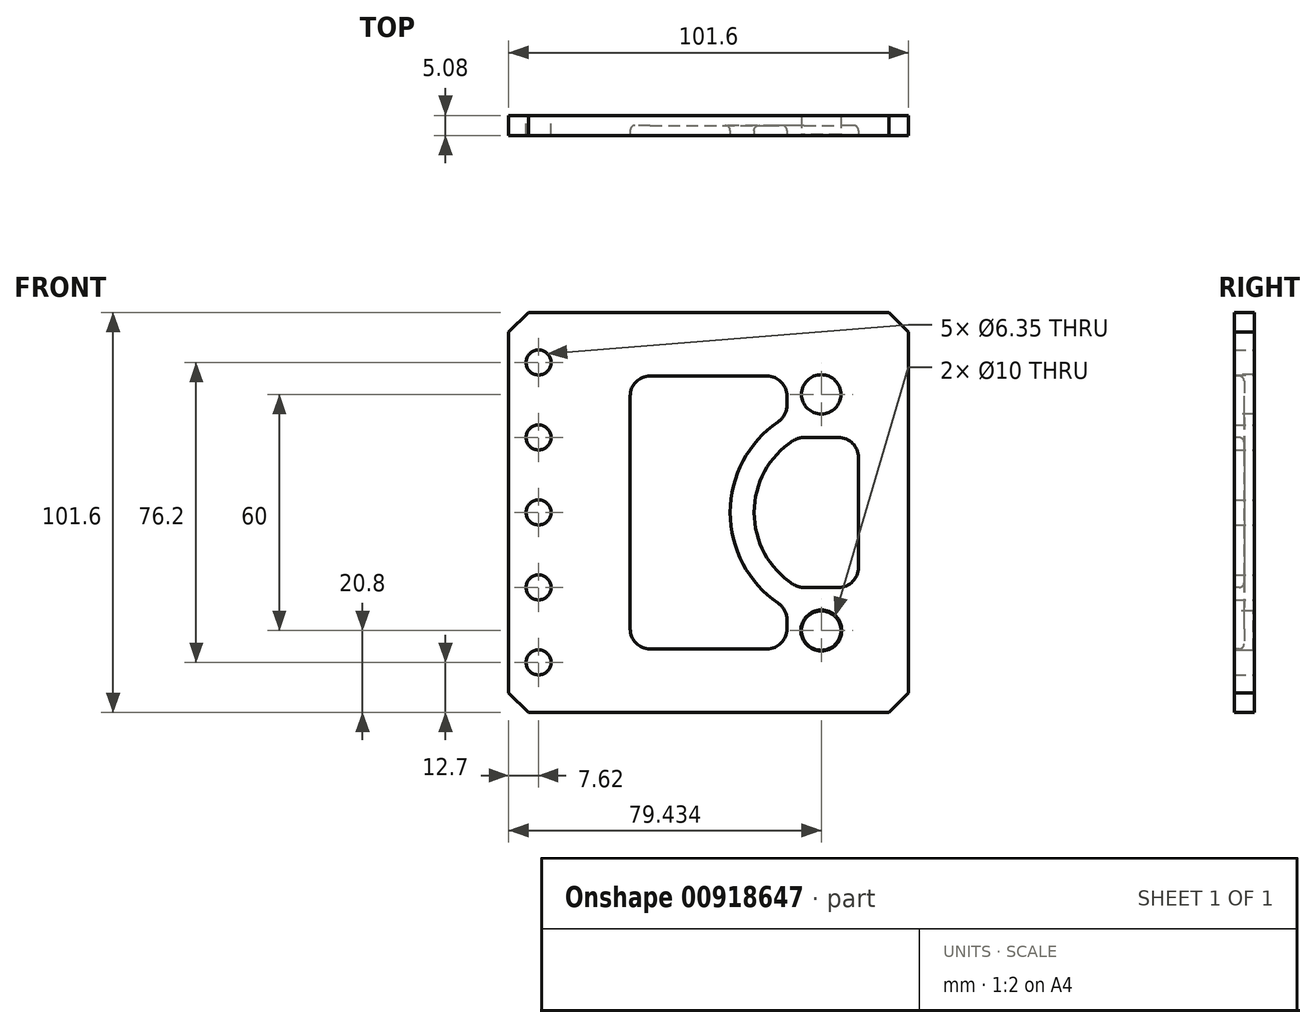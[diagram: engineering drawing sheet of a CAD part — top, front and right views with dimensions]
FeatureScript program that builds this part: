
annotation { "Feature Type Name" : "Feature", "Feature Type Description" : "" }
export const myFeature = defineFeature(function(context is Context, id is Id, definition is map)
    precondition{}
    {
        {
            var Q0;
            Q0=qCreatedBy(makeId("Front.planeOp"),FACE);
            var sketch = newSketch(context, id + "F0", { "sketchPlane" : qUnion([Q0])});
            skLineSegment(sketch, "E0.bottom", {"start": v(-50.8, -50.8) * mm, "end": v(50.8, -50.8) * mm});
            skLineSegment(sketch, "E0.top", {"start": v(-50.8, 50.8) * mm, "end": v(50.8, 50.8) * mm});
            skLineSegment(sketch, "E0.left", {"start": v(-50.8, -50.8) * mm, "end": v(-50.8, 50.8) * mm});
            skLineSegment(sketch, "E0.right", {"start": v(50.8, -50.8) * mm, "end": v(50.8, 50.8) * mm});
            skPoint(sketch, "E0.middle", {"position": v(0, 0) * mm});
            skSolve(sketch);
        }
        {
            var Q0;
            Q0 = qSketchRegion(id + "F0", true);
            extrude(context, id + "F1", {"entities" : qUnion([Q0]), "depth" : 5.08 * mm, "offsetDistance" : 25.4 * mm});
        }
        {
            var Q0;
            Q0=qCreatedBy(makeId("Front.planeOp"),FACE);
            var sketch = newSketch(context, id + "F2", { "sketchPlane" : qUnion([Q0])});
            skPoint(sketch, "E1", {"position": v(-43.18, 38.1) * mm});
            skPoint(sketch, "E2", {"position": v(-43.18, 19.05) * mm});
            skPoint(sketch, "E3", {"position": v(-43.18, 0) * mm});
            skPoint(sketch, "E4", {"position": v(-43.18, -19.05) * mm});
            skPoint(sketch, "E5", {"position": v(-43.18, -38.1) * mm});
            skLineSegment(sketch, "E6", {"start": v(-43.18, 38.1) * mm, "end": v(-43.18, 19.05) * mm, "construction": true});
            skLineSegment(sketch, "E7", {"start": v(-43.18, 19.05) * mm, "end": v(-43.18, 0) * mm, "construction": true});
            skLineSegment(sketch, "E8", {"start": v(-43.18, 0) * mm, "end": v(-43.18, -19.05) * mm, "construction": true});
            skLineSegment(sketch, "E9", {"start": v(-43.18, -19.05) * mm, "end": v(-43.18, -38.1) * mm, "construction": true});
            skSolve(sketch);
        }
        {
            var Q0;
            Q0=sQuery(id+"F2.wireOp",VERTEX,"E5");
            var Q1;
            Q1=sQuery(id+"F2.wireOp",VERTEX,"E4");
            var Q2;
            Q2=sQuery(id+"F2.wireOp",VERTEX,"E3");
            var Q3;
            Q3=sQuery(id+"F2.wireOp",VERTEX,"E2");
            var Q4;
            Q4=sQuery(id+"F2.wireOp",VERTEX,"E1");
            var Q5;
            Q5=makeQuery(id+"F1.opExtrude","SWEPT_BODY",BODY,{"disambiguationData":[OSD([sQuery(id+"F0.wireOp",EDGE,"E0.bottom"),sQuery(id+"F0.wireOp",EDGE,"E0.top"),sQuery(id+"F0.wireOp",EDGE,"E0.left"),sQuery(id+"F0.wireOp",EDGE,"E0.right")])]});
            hole(context, id + "F3", {"style" : HoleStyle.SIMPLE, "endStyle" : HoleEndStyle.THROUGH, "oppositeDirection" : true, "holeDiameter" : 6.35 * mm, "majorDiameter" : 6.35 * mm, "isTappedThrough" : true, "tappedDepth" : 12.7 * mm, "tapClearance" : 3, "locations" : qUnion([Q0, Q1, Q2, Q3, Q4]), "scope" : qUnion([Q5])});
        }
        {
            var Q0;
            Q0=makeQuery(id+"F1.opExtrude","CAP_FACE",FACE,{"disambiguationData":[OSD([sQuery(id+"F0.wireOp",EDGE,"E0.bottom"),sQuery(id+"F0.wireOp",EDGE,"E0.top"),sQuery(id+"F0.wireOp",EDGE,"E0.left"),sQuery(id+"F0.wireOp",EDGE,"E0.right")])],"isStart":false});
            var sketch = newSketch(context, id + "F4", { "sketchPlane" : qUnion([Q0])});
            skLineSegment(sketch, "E10.bottom", {"start": v(-19.92, -34.67) * mm, "end": v(19.92, -34.67) * mm});
            skLineSegment(sketch, "E10.top", {"start": v(-19.92, 34.67) * mm, "end": v(19.92, 34.67) * mm});
            skLineSegment(sketch, "E10.left", {"start": v(-19.92, -34.67) * mm, "end": v(-19.92, 34.67) * mm});
            skLineSegment(sketch, "E10.right", {"start": v(19.92, -34.67) * mm, "end": v(19.92, -24.4) * mm});
            skPoint(sketch, "E10.middle", {"position": v(0, 0) * mm});
            skArc(sketch, "E11", {"start": v(19.92, 24.4) * mm, "mid": v(5.49, 0) * mm, "end": v(19.92, -24.4) * mm});
            skLineSegment(sketch, "E12.trimOffspring", {"start": v(19.92, 24.4) * mm, "end": v(19.92, 34.67) * mm});
            skSolve(sketch);
        }
        {
            var Q0;
            Q0 = qSketchRegion(id + "F4", true);
            extrude(context, id + "F5", {"entities" : qUnion([Q0]), "operationType" : NewBodyOperationType.REMOVE, "oppositeDirection" : true, "depth" : 2.54 * mm, "offsetDistance" : 25.4 * mm});
        }
        {
            var Q0;
            Q0=makeQuery(id+"F5.boolean.opBoolean","COPY",EDGE,{"derivedFrom":makeQuery(id+"F5.opExtrude","SWEPT_EDGE",EDGE,{"disambiguationData":[OSD([sQuery(id+"F4.wireOp",EDGE,"E10.top"),sQuery(id+"F4.wireOp",EDGE,"E10.left")])]})});
            var Q1;
            Q1=makeQuery(id+"F5.boolean.opBoolean","COPY",EDGE,{"derivedFrom":makeQuery(id+"F5.opExtrude","SWEPT_EDGE",EDGE,{"disambiguationData":[OSD([sQuery(id+"F4.wireOp",EDGE,"E10.top"),sQuery(id+"F4.wireOp",EDGE,"E12.trimOffspring")])]})});
            var Q2;
            Q2=makeQuery(id+"F5.boolean.opBoolean","COPY",EDGE,{"derivedFrom":makeQuery(id+"F5.opExtrude","SWEPT_EDGE",EDGE,{"disambiguationData":[OSD([sQuery(id+"F4.wireOp",EDGE,"E11"),sQuery(id+"F4.wireOp",EDGE,"E12.trimOffspring")])]})});
            var Q3;
            Q3=makeQuery(id+"F5.boolean.opBoolean","COPY",EDGE,{"derivedFrom":makeQuery(id+"F5.opExtrude","SWEPT_EDGE",EDGE,{"disambiguationData":[OSD([sQuery(id+"F4.wireOp",EDGE,"E10.right"),sQuery(id+"F4.wireOp",EDGE,"E11")])]})});
            var Q4;
            Q4=makeQuery(id+"F5.boolean.opBoolean","COPY",EDGE,{"derivedFrom":makeQuery(id+"F5.opExtrude","SWEPT_EDGE",EDGE,{"disambiguationData":[OSD([sQuery(id+"F4.wireOp",EDGE,"E10.bottom"),sQuery(id+"F4.wireOp",EDGE,"E10.right")])]})});
            var Q5;
            Q5=makeQuery(id+"F5.boolean.opBoolean","COPY",EDGE,{"derivedFrom":makeQuery(id+"F5.opExtrude","SWEPT_EDGE",EDGE,{"disambiguationData":[OSD([sQuery(id+"F4.wireOp",EDGE,"E10.bottom"),sQuery(id+"F4.wireOp",EDGE,"E10.left")])]})});
            fillet(context, id + "F6", {"entities" : qUnion([Q0, Q1, Q2, Q3, Q4, Q5]), "radius" : 5.08 * mm, "tangentPropagation" : true, "allowEdgeOverflow" : false});
        }
        {
            var Q0;
            Q0=makeQuery(id+"F5.boolean.opBoolean","COPY",FACE,{"derivedFrom":makeQuery(id+"F5.opExtrude","CAP_FACE",FACE,{"disambiguationData":[OSD([sQuery(id+"F4.wireOp",EDGE,"E10.bottom"),sQuery(id+"F4.wireOp",EDGE,"E10.top"),sQuery(id+"F4.wireOp",EDGE,"E10.left"),sQuery(id+"F4.wireOp",EDGE,"E10.right"),sQuery(id+"F4.wireOp",EDGE,"E11"),sQuery(id+"F4.wireOp",EDGE,"E12.trimOffspring")])],"isStart":false})});
            fillet(context, id + "F7", {"entities" : qUnion([Q0]), "radius" : 1.27 * mm, "tangentPropagation" : true, "allowEdgeOverflow" : false});
        }
        {
            var Q0;
            Q0=makeQuery(id+"F1.opExtrude","CAP_FACE",FACE,{"disambiguationData":[OSD([sQuery(id+"F0.wireOp",EDGE,"E0.bottom"),sQuery(id+"F0.wireOp",EDGE,"E0.top"),sQuery(id+"F0.wireOp",EDGE,"E0.left"),sQuery(id+"F0.wireOp",EDGE,"E0.right")])],"isStart":false});
            var sketch = newSketch(context, id + "F8", { "sketchPlane" : qUnion([Q0])});
            skArc(sketch, "E13.0", {"start": v(22.85, 19.05) * mm, "mid": v(11.58, 0) * mm, "end": v(22.85, -19.05) * mm});
            skLineSegment(sketch, "E14", {"start": v(22.85, 19.05) * mm, "end": v(38.1, 19.05) * mm});
            skLineSegment(sketch, "E15", {"start": v(38.1, 19.05) * mm, "end": v(38.1, -19.05) * mm});
            skLineSegment(sketch, "E16", {"start": v(38.1, -19.05) * mm, "end": v(22.85, -19.05) * mm});
            skSolve(sketch);
        }
        {
            var Q0;
            Q0 = qSketchRegion(id + "F8", true);
            extrude(context, id + "F9", {"entities" : qUnion([Q0]), "operationType" : NewBodyOperationType.REMOVE, "oppositeDirection" : true, "depth" : 2.54 * mm, "offsetDistance" : 25.4 * mm});
        }
        {
            var Q0;
            Q0=makeQuery(id+"F9.boolean.opBoolean","COPY",EDGE,{"derivedFrom":makeQuery(id+"F9.opExtrude","SWEPT_EDGE",EDGE,{"disambiguationData":[OSD([sQuery(id+"F8.wireOp",EDGE,"E13.0"),sQuery(id+"F8.wireOp",EDGE,"E14")])]})});
            var Q1;
            Q1=makeQuery(id+"F9.boolean.opBoolean","COPY",EDGE,{"derivedFrom":makeQuery(id+"F9.opExtrude","SWEPT_EDGE",EDGE,{"disambiguationData":[OSD([sQuery(id+"F8.wireOp",EDGE,"E14"),sQuery(id+"F8.wireOp",EDGE,"E15")])]})});
            var Q2;
            Q2=makeQuery(id+"F9.boolean.opBoolean","COPY",EDGE,{"derivedFrom":makeQuery(id+"F9.opExtrude","SWEPT_EDGE",EDGE,{"disambiguationData":[OSD([sQuery(id+"F8.wireOp",EDGE,"E15"),sQuery(id+"F8.wireOp",EDGE,"E16")])]})});
            var Q3;
            Q3=makeQuery(id+"F9.boolean.opBoolean","COPY",EDGE,{"derivedFrom":makeQuery(id+"F9.opExtrude","SWEPT_EDGE",EDGE,{"disambiguationData":[OSD([sQuery(id+"F8.wireOp",EDGE,"E13.0"),sQuery(id+"F8.wireOp",EDGE,"E16")])]})});
            fillet(context, id + "F10", {"entities" : qUnion([Q0, Q1, Q2, Q3]), "radius" : 5.08 * mm, "tangentPropagation" : true, "allowEdgeOverflow" : false});
        }
        {
            var Q0;
            Q0=makeQuery(id+"F9.boolean.opBoolean","COPY",FACE,{"derivedFrom":makeQuery(id+"F9.opExtrude","CAP_FACE",FACE,{"disambiguationData":[OSD([sQuery(id+"F8.wireOp",EDGE,"E13.0"),sQuery(id+"F8.wireOp",EDGE,"E14"),sQuery(id+"F8.wireOp",EDGE,"E15"),sQuery(id+"F8.wireOp",EDGE,"E16")])],"isStart":false})});
            fillet(context, id + "F11", {"entities" : qUnion([Q0]), "radius" : 1.27 * mm, "tangentPropagation" : true, "allowEdgeOverflow" : false});
        }
        {
            var Q0;
            Q0=makeQuery(id+"F1.opExtrude","CAP_FACE",FACE,{"disambiguationData":[OSD([sQuery(id+"F0.wireOp",EDGE,"E0.bottom"),sQuery(id+"F0.wireOp",EDGE,"E0.top"),sQuery(id+"F0.wireOp",EDGE,"E0.left"),sQuery(id+"F0.wireOp",EDGE,"E0.right")])],"isStart":false});
            var sketch = newSketch(context, id + "F12", { "sketchPlane" : qUnion([Q0])});
            skCircle(sketch, "E17", {"center": v(28.63, 30) * mm, "radius": 5 * mm});
            skCircle(sketch, "E18", {"center": v(28.63, -30) * mm, "radius": 5 * mm});
            skPoint(sketch, "E18.centerSnap0", {"position": v(28.63, -19.05) * mm});
            skLineSegment(sketch, "E19.0.1", {"start": v(-50.8, 50.8) * mm, "end": v(-50.8, -50.8) * mm, "construction": true});
            skLineSegment(sketch, "E19.0.2", {"start": v(-50.8, -50.8) * mm, "end": v(50.8, -50.8) * mm, "construction": true});
            skLineSegment(sketch, "E19.0.3", {"start": v(50.8, -50.8) * mm, "end": v(50.8, 50.8) * mm, "construction": true});
            skLineSegment(sketch, "E20", {"start": v(28.63, 30) * mm, "end": v(28.63, 0) * mm, "construction": true});
            skLineSegment(sketch, "E21", {"start": v(28.63, 0) * mm, "end": v(28.63, -30) * mm, "construction": true});
            skSolve(sketch);
        }
        {
            var Q0;
            Q0 = qSketchRegion(id + "F12", true);
            extrude(context, id + "F13", {"entities" : qUnion([Q0]), "operationType" : NewBodyOperationType.REMOVE, "oppositeDirection" : true, "depth" : 25 * mm, "offsetDistance" : 25 * mm});
        }
        {
            var Q0;
            Q0=makeQuery(id+"F13.boolean.opBoolean","COPY",EDGE,{"derivedFrom":makeQuery(id+"F13.opExtrude","CAP_EDGE",EDGE,{"disambiguationData":[OSD([sQuery(id+"F12.wireOp",EDGE,"E17")])],"isStart":true})});
            var Q1;
            Q1=makeQuery(id+"F13.boolean.opBoolean","COPY",FACE,{"derivedFrom":makeQuery(id+"F13.opExtrude","SWEPT_FACE",FACE,{"disambiguationData":[OSD([sQuery(id+"F12.wireOp",EDGE,"E18")])]})});
            chamfer(context, id + "F14", {"entities" : qUnion([Q0, Q1]), "width" : 0.2 * mm, "tangentPropagation" : true});
        }
        {
            var Q0;
            Q0=makeQuery(id+"F1.opExtrude","SWEPT_EDGE",EDGE,{"disambiguationData":[OSD([sQuery(id+"F0.wireOp",EDGE,"E0.bottom"),sQuery(id+"F0.wireOp",EDGE,"E0.right")])]});
            var Q1;
            Q1=makeQuery(id+"F1.opExtrude","SWEPT_EDGE",EDGE,{"disambiguationData":[OSD([sQuery(id+"F0.wireOp",EDGE,"E0.top"),sQuery(id+"F0.wireOp",EDGE,"E0.right")])]});
            var Q2;
            Q2=makeQuery(id+"F1.opExtrude","SWEPT_EDGE",EDGE,{"disambiguationData":[OSD([sQuery(id+"F0.wireOp",EDGE,"E0.bottom"),sQuery(id+"F0.wireOp",EDGE,"E0.left")])]});
            var Q3;
            Q3=makeQuery(id+"F1.opExtrude","SWEPT_EDGE",EDGE,{"disambiguationData":[OSD([sQuery(id+"F0.wireOp",EDGE,"E0.top"),sQuery(id+"F0.wireOp",EDGE,"E0.left")])]});
            chamfer(context, id + "F15", {"entities" : qUnion([Q0, Q1, Q2, Q3]), "width" : 5 * mm, "tangentPropagation" : true});
        }
    });
